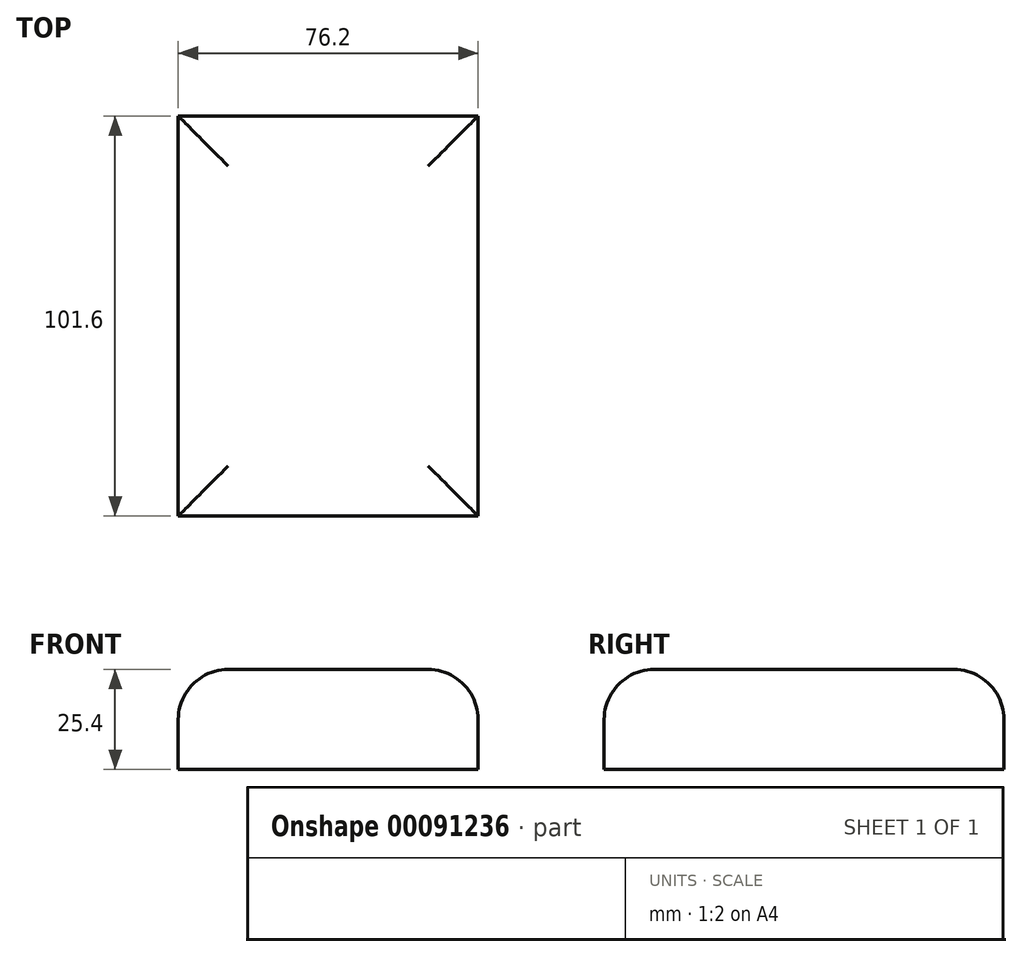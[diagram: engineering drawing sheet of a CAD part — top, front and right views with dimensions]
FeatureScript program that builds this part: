
annotation { "Feature Type Name" : "Feature", "Feature Type Description" : "" }
export const myFeature = defineFeature(function(context is Context, id is Id, definition is map)
    precondition{}
    {
        {
            var Q0;
            Q0=qCreatedBy(makeId("Top.planeOp"),FACE);
            var sketch = newSketch(context, id + "F0", { "sketchPlane" : qUnion([Q0])});
            skLineSegment(sketch, "E0.bottom", {"start": v(-38.1, 50.8) * mm, "end": v(38.1, 50.8) * mm});
            skLineSegment(sketch, "E0.top", {"start": v(-38.1, -50.8) * mm, "end": v(38.1, -50.8) * mm});
            skLineSegment(sketch, "E0.left", {"start": v(-38.1, 50.8) * mm, "end": v(-38.1, -50.8) * mm});
            skLineSegment(sketch, "E0.right", {"start": v(38.1, 50.8) * mm, "end": v(38.1, -50.8) * mm});
            skPoint(sketch, "E0.middle", {"position": v(0, 0) * mm});
            skSolve(sketch);
        }
        {
            var Q0;
            Q0 = qSketchRegion(id + "F0", true);
            extrude(context, id + "F1", {"entities" : qUnion([Q0]), "endBound" : BoundingType.SYMMETRIC, "depth" : 25.4 * mm});
        }
        {
            var Q0;
            Q0=makeQuery(id+"F1.opExtrude","CAP_EDGE",EDGE,{"disambiguationData":[OSD([sQuery(id+"F0.wireOp",EDGE,"E0.top")])],"isStart":false});
            var Q1;
            Q1=makeQuery(id+"F1.opExtrude","CAP_EDGE",EDGE,{"disambiguationData":[OSD([sQuery(id+"F0.wireOp",EDGE,"E0.right")])],"isStart":false});
            var Q2;
            Q2=makeQuery(id+"F1.opExtrude","CAP_EDGE",EDGE,{"disambiguationData":[OSD([sQuery(id+"F0.wireOp",EDGE,"E0.left")])],"isStart":false});
            var Q3;
            Q3=makeQuery(id+"F1.opExtrude","CAP_EDGE",EDGE,{"disambiguationData":[OSD([sQuery(id+"F0.wireOp",EDGE,"E0.bottom")])],"isStart":false});
            fillet(context, id + "F2", {"entities" : qUnion([Q0, Q1, Q2, Q3]), "radius" : 12.7 * mm, "tangentPropagation" : true, "allowEdgeOverflow" : false});
        }
    });
